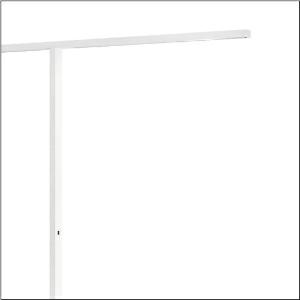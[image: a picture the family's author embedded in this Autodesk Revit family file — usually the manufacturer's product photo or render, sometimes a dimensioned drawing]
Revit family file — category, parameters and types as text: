
# Revit family: silica_r__11_floor_duo_5mx51bs8wzk00006xx_4f95
name_source: partatom
category: Lighting Fixtures
units: mm (PartAtom-declared; Revit-internal decimal feet)

## family parameters
Cut with Voids When Loaded = No
Host = Face
Light Source = No
Part Type = Normal
Room Calculation Point = No
Round Connector Dimension = Use Diameter
Shared = No

## types (1)
- --- (1 x LED, 3970 lm / 8500 lm, 24.1 W / 53.2 W, 4000K)
    Apparent Load = 155 VA
    CIE Flux Codes = 82 97 100 100 100 / - - - 0 100
    Color Rendering = 80
    Color Temperature = 4000K
    Default Elevation = 1800 mm
    Description = Silica® 11 Floor duo, floorstanding luminaire, of PMMA, primary optical cover: cover panel, of PMMA, light emission: indirect/direct distribution, primary light characteristic: symmetric, installation type: not mounted, LED, rated luminous flux: 24.930lm, luminous efficacy: 161lm/W, light colour: 840, colour temperature: 4000K, daylight-dependent control, mains connection: 230V, AC, 50Hz, connection cable pre-assembled, cable length: 3m, rated input power: 155W, luminaire head, rectangular, rounded, of aluminium, coated, traffic white (RAL 9016), supporting column, angular, of aluminium, coated, traffic white (RAL 9016), baseplate, of steel, coated, traffic white (RAL 9016), length: 2.598mm, width: 65mm, protection rating (complete): IP20, insulation class (complete): insulation class I (protective earthing), certification: CE, permissible operating ambient temperature: 0..+35°C, standard: EN 50419, packaging unit: 1 piece
    Height = 40 mm  [stored 0.131234 ft]
    Lamp = 1 x LED
    Lamp Light Flux = 3970 lm / 8500 lm
    Lamp Power = 24.1 W / 53.2 W
    Lamp count = 1
    Length = 2598 mm
    Luminous efficacy = 161 lm/W
    Manufacturer = Siteco
    ModVariant = No
    Model = 5MX51BS8WZK00006XX
    Mounting Place = Floor
    Mounting Type = Freestanding
    Number of Poles = 1
    OnlyDefault = Yes
    Power Factor = 1
    Product Name = Silica® 11 Floor duo
    Product group = floorstanding luminaire
    ProductGroupID = 1301
    Protection Class = Protection class I
    Protection Degree = IP 20
    RLX_Detail_Level = 1
    RLX_Emergency_Light_Flux = 0 lm
    RLX_Emergency_Type = 0
    RLX_Emergency_Type_DB = No
    RlxData = <blob elided: 19161 chars, md5=88071bd1>
    Socket = socket
    Standby Power = 0 W
    System Light Flux = 24940 lm
    System Power = 155 W
    Type Comments = factory setting: direct and indirect light
    Type Image = l_1004652.jpg
    URL = http://relux.com
    VarID = @adj_140097
    Voltage = 0 V
    Weight = 0.00 kg
    Width = 65 mm

note: [stored X ft] marks values corroborated as IEEE doubles in the binary element streams (Revit-internal decimal feet)

## geometry (parser evidence)
native form markers: Blend x4, Sweep x21
no freeform markers — native parametric forms only
